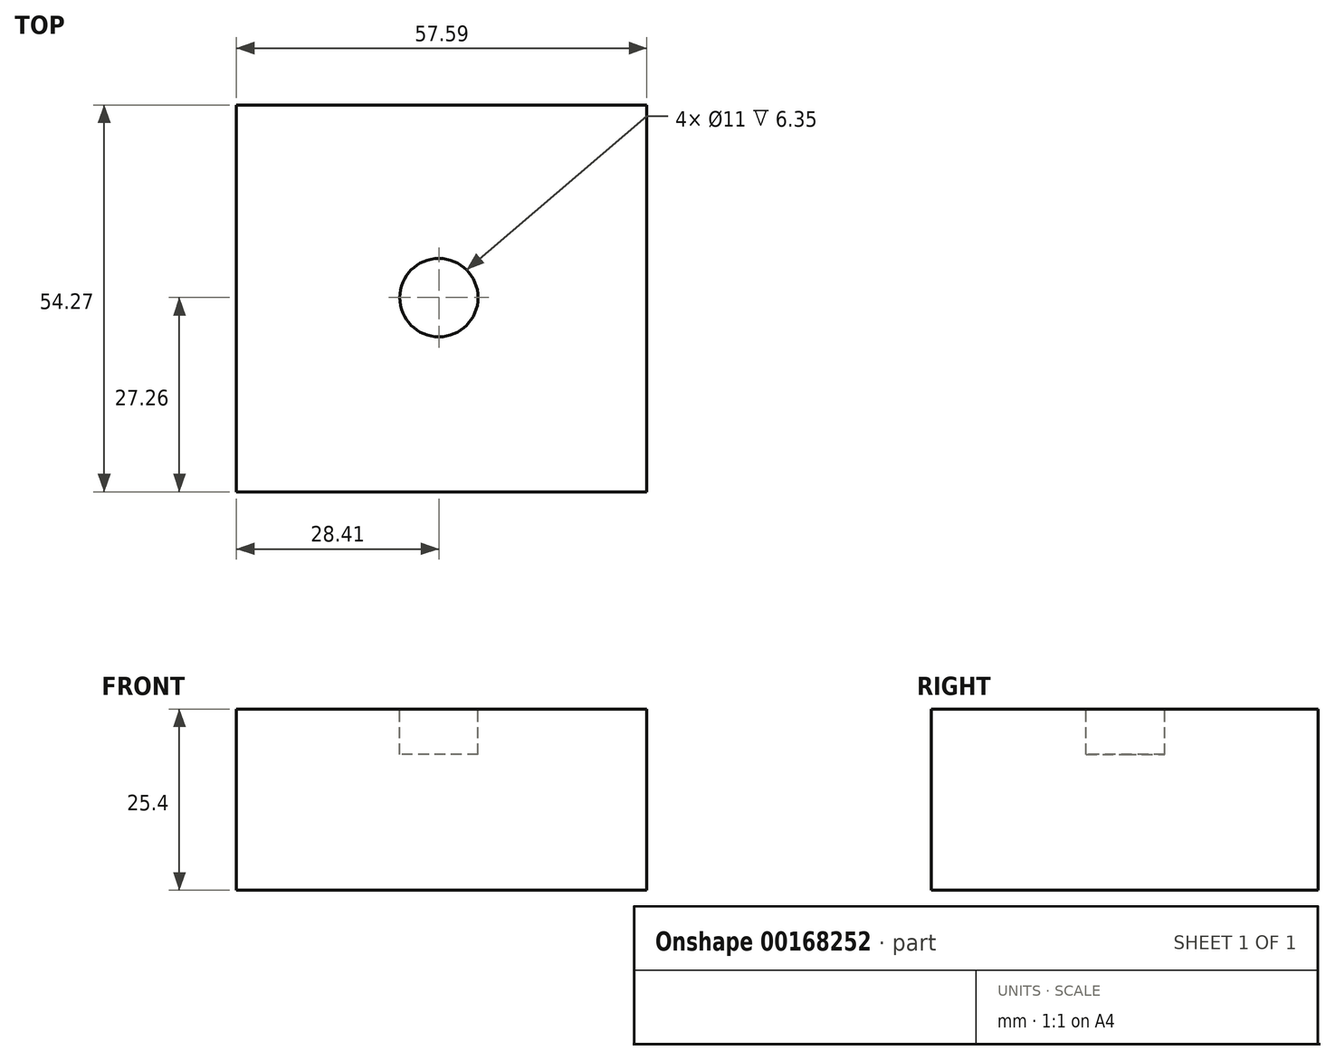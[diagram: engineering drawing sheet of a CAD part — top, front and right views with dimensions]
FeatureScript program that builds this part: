
annotation { "Feature Type Name" : "Feature", "Feature Type Description" : "" }
export const myFeature = defineFeature(function(context is Context, id is Id, definition is map)
    precondition{}
    {
        {
            var Q0;
            Q0=qCreatedBy(makeId("Top.planeOp"),FACE);
            var sketch = newSketch(context, id + "F0", { "sketchPlane" : qUnion([Q0])});
            skCircle(sketch, "E0", {"center": v(0, 0) * mm, "radius": 5.5 * mm});
            skLineSegment(sketch, "E1.bottom", {"start": v(-28.41, 27) * mm, "end": v(29.18, 27) * mm});
            skLineSegment(sketch, "E1.top", {"start": v(-28.41, -27.26) * mm, "end": v(29.18, -27.26) * mm});
            skLineSegment(sketch, "E1.left", {"start": v(-28.41, 27) * mm, "end": v(-28.41, -27.26) * mm});
            skLineSegment(sketch, "E1.right", {"start": v(29.18, 27) * mm, "end": v(29.18, -27.26) * mm});
            skSolve(sketch);
        }
        {
            var Q0;
            Q0=makeQuery(id+"F0.imprint","IMPRINT",FACE,{"disambiguationData":[TD([[makeQuery(id+"F0.imprint","IMPRINT",EDGE,{"derivedFrom":sQuery(id+"F0.wireOp",EDGE,"E0")}),-1.0]])]});
            var Q1;
            Q1=makeQuery(id+"F0.imprint","IMPRINT",FACE,{"disambiguationData":[TD([[makeQuery(id+"F0.imprint","IMPRINT",EDGE,{"derivedFrom":sQuery(id+"F0.wireOp",EDGE,"E0")}),1.0]])]});
            extrude(context, id + "F1", {"entities" : qUnion([Q0, Q1]), "depth" : 25.4 * mm});
        }
        {
            var Q0;
            Q0=makeQuery(id+"F1.opExtrude","CAP_FACE",FACE,{"disambiguationData":[OSD([sQuery(id+"F0.wireOp",EDGE,"E1.bottom"),sQuery(id+"F0.wireOp",EDGE,"E1.top"),sQuery(id+"F0.wireOp",EDGE,"E1.left"),sQuery(id+"F0.wireOp",EDGE,"E1.right")])],"isStart":false});
            var sketch = newSketch(context, id + "F2", { "sketchPlane" : qUnion([Q0])});
            skCircle(sketch, "E2", {"center": v(0, 0) * mm, "radius": 5.5 * mm});
            skSolve(sketch);
        }
        {
            var Q0;
            Q0=makeQuery(id+"F2.imprint","IMPRINT",FACE,{"disambiguationData":[TD([[makeQuery(id+"F2.imprint","IMPRINT",EDGE,{"derivedFrom":sQuery(id+"F2.wireOp",EDGE,"E2")}),1.0]])]});
            extrude(context, id + "F3", {"entities" : qUnion([Q0]), "operationType" : NewBodyOperationType.REMOVE, "oppositeDirection" : true, "depth" : 6.35 * mm});
        }
    });
